# Revit family: WALL WASHER LIGHTBAR_LKT24RGB
name_source: partatom
category: Luminarias
units: mm (PartAtom-declared; Revit-internal decimal feet)

## family parameters
Compartido = No
Corte con vacíos al cargar = No
Cota de conector redondo = Diámetro de uso
Origen de luz = Sí
Punto de cálculo de habitación = No
Se basa en plano de trabajo = Sí
Siempre vertical = No
Tipo de pieza = Normal

## types (1)
- REFL_LKT24RGB
    Cambio de temperatura de color de luz atenuada = Curva de lámpara incandescente
    Comentarios de vataje = 24V
    Descripción = LUMINARIA TIPO REFLECTOR LINEAL, WALL WASHER , CUERPO EN ALUMINIO EXTRUIDO ANODIZADO, CUENTA CON 36 LED TIPO RGB CON UN CONSUMO TOTAL DE 43W, 2016 LUMENES, RGB, IP 65, CABLE DE 1M, APERTURA SEGUN PROYECTO, ALIMENTADA A 24V. REQUIERE ACCESORIOS.
    Elevación por defecto = 0 mm  [stored 0 ft]
    Fabricante = BRILLANT
    Filtro de color = 16777215
    Longitud de línea de emisión = 400 mm  [stored 1.31234 ft]
    Longitud de símbolo de origen de luz = 500 mm  [stored 1.64042 ft]
    Lámpara = RGB
    Modelo = LKT24RGB
    Watt per fixture = 43
    Ángulo de campo de foco = 15.00°
    Ángulo de enfoque = 15.00°
    Ángulo de inclinación = 3.00°

note: [stored X ft] marks values corroborated as IEEE doubles in the binary element streams (Revit-internal decimal feet)

## geometry (parser evidence)
native form markers: Blend x2
no freeform markers — native parametric forms only
